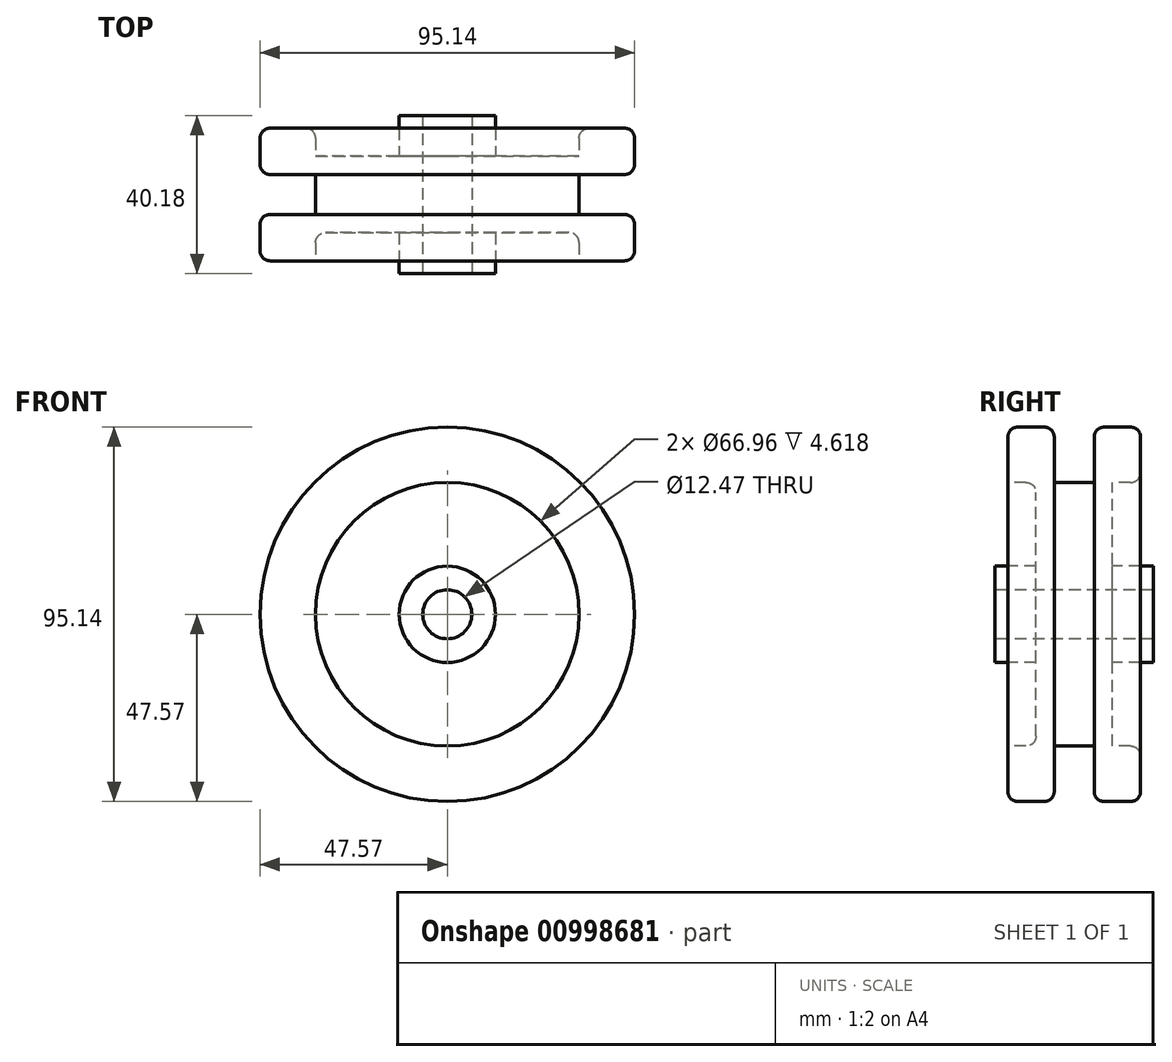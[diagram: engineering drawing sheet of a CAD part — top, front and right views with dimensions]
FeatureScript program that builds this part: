
annotation { "Feature Type Name" : "Feature", "Feature Type Description" : "" }
export const myFeature = defineFeature(function(context is Context, id is Id, definition is map)
    precondition{}
    {
        {
            var Q0;
            Q0=qCreatedBy(makeId("Right.planeOp"),FACE);
            var sketch = newSketch(context, id + "F0", { "sketchPlane" : qUnion([Q0])});
            skLineSegment(sketch, "E0", {"start": v(-72.74, 0) * mm, "end": v(70.66, 0) * mm, "construction": true});
            skLineSegment(sketch, "E1", {"start": v(0, -72.27) * mm, "end": v(0, 72.5) * mm, "construction": true});
            skLineSegment(sketch, "E2", {"start": v(0, 6.23) * mm, "end": v(-20.09, 6.23) * mm});
            skLineSegment(sketch, "E3", {"start": v(-20.09, 6.23) * mm, "end": v(-20.09, 12.24) * mm});
            skLineSegment(sketch, "E4", {"start": v(-20.09, 12.24) * mm, "end": v(-9.7, 12.24) * mm});
            skLineSegment(sketch, "E5", {"start": v(-9.7, 12.24) * mm, "end": v(-9.7, 30.94) * mm});
            skLineSegment(sketch, "E6", {"start": v(-12.24, 33.48) * mm, "end": v(-16.86, 33.48) * mm});
            skLineSegment(sketch, "E7", {"start": v(-16.86, 33.48) * mm, "end": v(-16.86, 45.03) * mm});
            skLineSegment(sketch, "E8", {"start": v(-14.32, 47.57) * mm, "end": v(-7.62, 47.57) * mm});
            skLineSegment(sketch, "E9", {"start": v(-5.08, 45.03) * mm, "end": v(-5.08, 33.48) * mm});
            skLineSegment(sketch, "E10", {"start": v(-5.08, 33.48) * mm, "end": v(0, 33.48) * mm});
            skLineSegment(sketch, "E11.MirrorCS", {"start": v(5.08, 45.03) * mm, "end": v(5.08, 33.48) * mm});
            skLineSegment(sketch, "E12.MirrorCS", {"start": v(5.08, 33.48) * mm, "end": v(0, 33.48) * mm});
            skLineSegment(sketch, "E13.MirrorCS", {"start": v(14.32, 47.57) * mm, "end": v(7.62, 47.57) * mm});
            skLineSegment(sketch, "E14.MirrorCS", {"start": v(16.86, 36.02) * mm, "end": v(16.86, 45.03) * mm});
            skLineSegment(sketch, "E15.MirrorCS", {"start": v(9.7, 33.48) * mm, "end": v(14.32, 33.48) * mm});
            skLineSegment(sketch, "E16.MirrorCS", {"start": v(9.7, 12.24) * mm, "end": v(9.7, 33.48) * mm});
            skLineSegment(sketch, "E17.MirrorCS", {"start": v(20.09, 12.24) * mm, "end": v(9.7, 12.24) * mm});
            skLineSegment(sketch, "E18.MirrorCS", {"start": v(20.09, 6.23) * mm, "end": v(20.09, 12.24) * mm});
            skLineSegment(sketch, "E19.MirrorCS", {"start": v(0, 6.23) * mm, "end": v(20.09, 6.23) * mm});
            skPoint(sketch, "E20.visualSharp", {"position": v(16.86, 47.57) * mm});
            skArc(sketch, "E20.filletArc", {"start": v(16.86, 45.03) * mm, "mid": v(16.11, 46.82) * mm, "end": v(14.32, 47.57) * mm});
            skPoint(sketch, "E21.visualSharp", {"position": v(5.08, 47.57) * mm});
            skArc(sketch, "E21.filletArc", {"start": v(7.62, 47.57) * mm, "mid": v(5.82, 46.82) * mm, "end": v(5.08, 45.03) * mm});
            skPoint(sketch, "E22.visualSharp", {"position": v(-5.08, 47.57) * mm});
            skArc(sketch, "E22.filletArc", {"start": v(-5.08, 45.03) * mm, "mid": v(-5.82, 46.82) * mm, "end": v(-7.62, 47.57) * mm});
            skPoint(sketch, "E23.visualSharp", {"position": v(-16.86, 47.57) * mm});
            skArc(sketch, "E23.filletArc", {"start": v(-14.32, 47.57) * mm, "mid": v(-16.11, 46.82) * mm, "end": v(-16.86, 45.03) * mm});
            skPoint(sketch, "E24.visualSharp", {"position": v(16.86, 33.48) * mm});
            skArc(sketch, "E24.filletArc", {"start": v(14.32, 33.48) * mm, "mid": v(16.11, 34.23) * mm, "end": v(16.86, 36.02) * mm});
            skPoint(sketch, "E25.visualSharp", {"position": v(-9.7, 33.48) * mm});
            skArc(sketch, "E25.filletArc", {"start": v(-9.7, 30.94) * mm, "mid": v(-10.44, 32.74) * mm, "end": v(-12.24, 33.48) * mm});
            skSolve(sketch);
        }
        {
            var Q0;
            Q0 = qSketchRegion(id + "F0", true);
            var Q1;
            Q1=sQuery(id+"F0.wireOp",EDGE,"E0");
            revolve(context, id + "F1", {"surfaceOperationType" : NewSurfaceOperationType.NEW, "entities" : qUnion([Q0]), "axis" : qUnion([Q1]), "revolveType" : RevolveType.ONE_DIRECTION, "angle" : 360 * degree});
        }
    });
